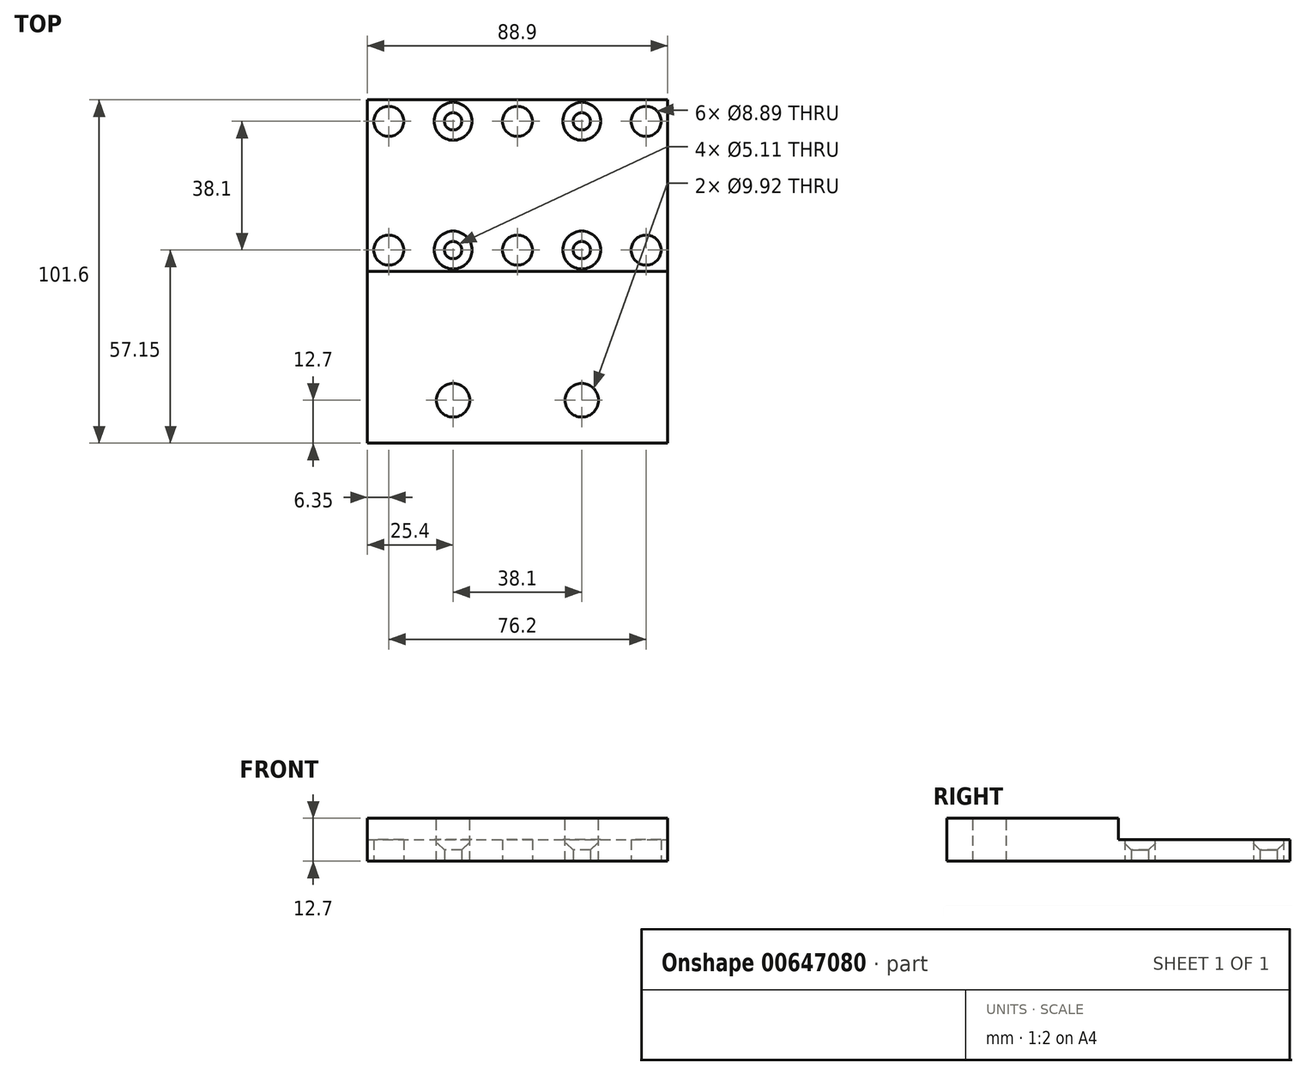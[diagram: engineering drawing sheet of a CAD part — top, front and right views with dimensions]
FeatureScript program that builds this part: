
annotation { "Feature Type Name" : "Feature", "Feature Type Description" : "" }
export const myFeature = defineFeature(function(context is Context, id is Id, definition is map)
    precondition{}
    {
        {
            var Q0;
            Q0=qCreatedBy(makeId("Top.planeOp"),FACE);
            var sketch = newSketch(context, id + "F0", { "sketchPlane" : qUnion([Q0])});
            skLineSegment(sketch, "E0.bottom", {"start": v(-44.45, 50.8) * mm, "end": v(44.45, 50.8) * mm});
            skLineSegment(sketch, "E0.top", {"start": v(-44.45, -50.8) * mm, "end": v(44.45, -50.8) * mm});
            skLineSegment(sketch, "E0.left", {"start": v(-44.45, 50.8) * mm, "end": v(-44.45, -50.8) * mm});
            skLineSegment(sketch, "E0.right", {"start": v(44.45, 50.8) * mm, "end": v(44.45, -50.8) * mm});
            skPoint(sketch, "E1", {"position": v(-44.45, 0) * mm});
            skPoint(sketch, "E2", {"position": v(0, 50.8) * mm});
            skCircle(sketch, "E3", {"center": v(-38.1, 44.45) * mm, "radius": 4.45 * mm});
            skCircle(sketch, "E4", {"center": v(0, 44.45) * mm, "radius": 4.45 * mm});
            skCircle(sketch, "E5", {"center": v(38.1, 44.45) * mm, "radius": 4.45 * mm});
            skCircle(sketch, "E6", {"center": v(-38.1, 6.35) * mm, "radius": 4.45 * mm});
            skCircle(sketch, "E7", {"center": v(0, 6.35) * mm, "radius": 4.45 * mm});
            skCircle(sketch, "E8", {"center": v(38.1, 6.35) * mm, "radius": 4.45 * mm});
            skLineSegment(sketch, "E9", {"start": v(19.05, 50.8) * mm, "end": v(19.05, 0) * mm, "construction": true});
            skLineSegment(sketch, "E10", {"start": v(-19.05, 50.8) * mm, "end": v(-19.05, 0) * mm, "construction": true});
            skCircle(sketch, "E11", {"center": v(19.05, 44.45) * mm, "radius": 2.55 * mm});
            skCircle(sketch, "E12", {"center": v(19.05, 6.35) * mm, "radius": 2.55 * mm});
            skCircle(sketch, "E13", {"center": v(-19.05, 6.35) * mm, "radius": 2.55 * mm});
            skCircle(sketch, "E14", {"center": v(-19.05, 44.45) * mm, "radius": 2.55 * mm});
            skSolve(sketch);
        }
        {
            var Q0;
            Q0 = qSketchRegion(id + "F0", true);
            extrude(context, id + "F1", {"entities" : qUnion([Q0]), "depth" : 6.35 * mm, "offsetDistance" : 25.4 * mm});
        }
        {
            var Q0;
            Q0=makeQuery(id+"F1.opExtrude","CAP_FACE",FACE,{"disambiguationData":[OSD([sQuery(id+"F0.wireOp",EDGE,"E0.bottom"),sQuery(id+"F0.wireOp",EDGE,"E0.top"),sQuery(id+"F0.wireOp",EDGE,"E0.left"),sQuery(id+"F0.wireOp",EDGE,"E0.right"),sQuery(id+"F0.wireOp",EDGE,"E3"),sQuery(id+"F0.wireOp",EDGE,"E4"),sQuery(id+"F0.wireOp",EDGE,"E5"),sQuery(id+"F0.wireOp",EDGE,"E6"),sQuery(id+"F0.wireOp",EDGE,"E7"),sQuery(id+"F0.wireOp",EDGE,"E8"),sQuery(id+"F0.wireOp",EDGE,"E11"),sQuery(id+"F0.wireOp",EDGE,"E12"),sQuery(id+"F0.wireOp",EDGE,"E13"),sQuery(id+"F0.wireOp",EDGE,"E14")])],"isStart":false});
            var sketch = newSketch(context, id + "F2", { "sketchPlane" : qUnion([Q0])});
            skLineSegment(sketch, "E15.bottom", {"start": v(-44.45, 0) * mm, "end": v(44.45, 0) * mm});
            skLineSegment(sketch, "E15.top", {"start": v(-44.45, -50.8) * mm, "end": v(44.45, -50.8) * mm});
            skLineSegment(sketch, "E15.left", {"start": v(-44.45, 0) * mm, "end": v(-44.45, -50.8) * mm});
            skLineSegment(sketch, "E15.right", {"start": v(44.45, 0) * mm, "end": v(44.45, -50.8) * mm});
            skSolve(sketch);
        }
        {
            var Q0;
            Q0 = qSketchRegion(id + "F2", true);
            extrude(context, id + "F3", {"entities" : qUnion([Q0]), "operationType" : NewBodyOperationType.ADD, "depth" : 6.35 * mm, "offsetDistance" : 25.4 * mm});
        }
        {
            var Q0;
            Q0=makeQuery(id+"F3.opExtrude","CAP_FACE",FACE,{"disambiguationData":[OSD([sQuery(id+"F2.wireOp",EDGE,"E15.bottom"),sQuery(id+"F2.wireOp",EDGE,"E15.top"),sQuery(id+"F2.wireOp",EDGE,"E15.left"),sQuery(id+"F2.wireOp",EDGE,"E15.right")])],"isStart":false});
            var sketch = newSketch(context, id + "F4", { "sketchPlane" : qUnion([Q0])});
            skLineSegment(sketch, "E16", {"start": v(0, 0) * mm, "end": v(0, -50.8) * mm, "construction": true});
            skPoint(sketch, "E17.centerSnap0", {"position": v(0, -25.4) * mm});
            skCircle(sketch, "E18", {"center": v(-19.05, -38.1) * mm, "radius": 4.96 * mm});
            skCircle(sketch, "E19", {"center": v(19.05, -38.1) * mm, "radius": 4.96 * mm});
            skSolve(sketch);
        }
        {
            var Q0;
            Q0 = qSketchRegion(id + "F4", true);
            extrude(context, id + "F5", {"entities" : qUnion([Q0]), "operationType" : NewBodyOperationType.REMOVE, "oppositeDirection" : true, "depth" : 25.4 * mm, "offsetDistance" : 25.4 * mm});
        }
        {
            var Q0;
            Q0=makeQuery(id+"F1.opExtrude","CAP_EDGE",EDGE,{"disambiguationData":[OSD([sQuery(id+"F0.wireOp",EDGE,"E14")])],"isStart":false});
            var Q1;
            Q1=makeQuery(id+"F1.opExtrude","CAP_EDGE",EDGE,{"disambiguationData":[OSD([sQuery(id+"F0.wireOp",EDGE,"E11")])],"isStart":false});
            var Q2;
            Q2=makeQuery(id+"F1.opExtrude","CAP_EDGE",EDGE,{"disambiguationData":[OSD([sQuery(id+"F0.wireOp",EDGE,"E12")])],"isStart":false});
            var Q3;
            Q3=makeQuery(id+"F1.opExtrude","CAP_EDGE",EDGE,{"disambiguationData":[OSD([sQuery(id+"F0.wireOp",EDGE,"E13")])],"isStart":false});
            chamfer(context, id + "F6", {"entities" : qUnion([Q0, Q1, Q2, Q3]), "width" : 3.05 * mm, "tangentPropagation" : true});
        }
    });
